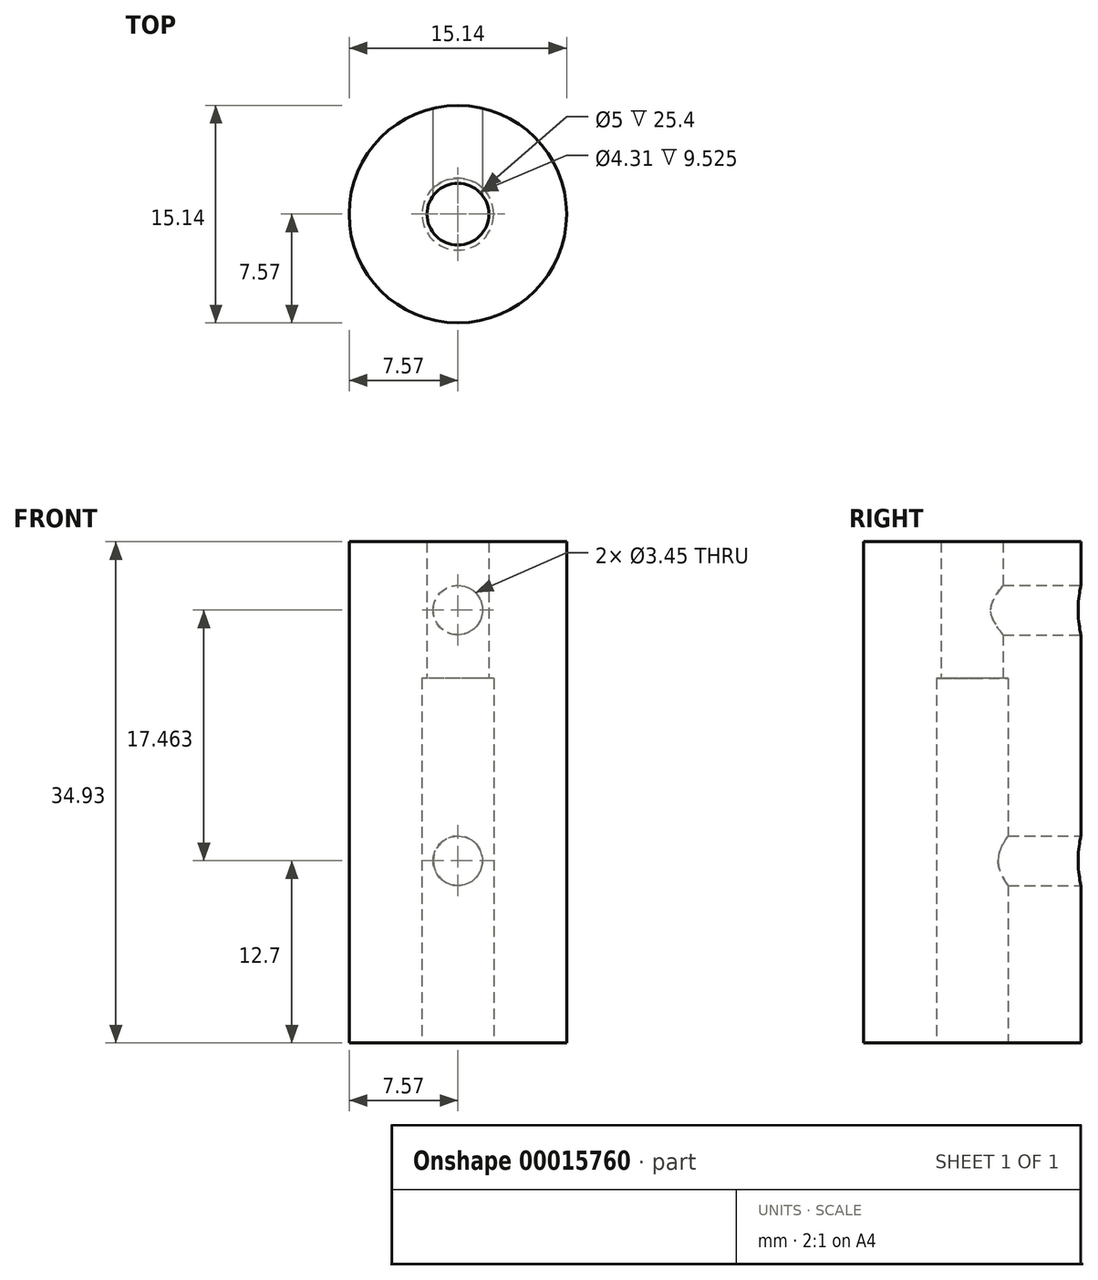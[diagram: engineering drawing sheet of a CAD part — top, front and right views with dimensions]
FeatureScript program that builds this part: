
annotation { "Feature Type Name" : "Feature", "Feature Type Description" : "" }
export const myFeature = defineFeature(function(context is Context, id is Id, definition is map)
    precondition{}
    {
        {
            var Q0;
            Q0=qCreatedBy(makeId("Top.planeOp"),FACE);
            var sketch = newSketch(context, id + "F0", { "sketchPlane" : qUnion([Q0])});
            skLineSegment(sketch, "E0.bottom", {"start": v(7.57, -7.57) * mm, "end": v(-7.57, -7.57) * mm});
            skLineSegment(sketch, "E0.top", {"start": v(7.57, 7.57) * mm, "end": v(-7.57, 7.57) * mm});
            skLineSegment(sketch, "E0.left", {"start": v(7.57, -7.57) * mm, "end": v(7.57, 7.57) * mm});
            skLineSegment(sketch, "E0.right", {"start": v(-7.57, -7.57) * mm, "end": v(-7.57, 7.57) * mm});
            skPoint(sketch, "E0.middle", {"position": v(0, 0) * mm});
            skCircle(sketch, "E1", {"center": v(0, 0) * mm, "radius": 7.57 * mm, "construction": true});
            skCircle(sketch, "E2", {"center": v(0, 0) * mm, "radius": 2.5 * mm});
            skLineSegment(sketch, "E3.bottom", {"start": v(2.15, 2.5) * mm, "end": v(-2.15, 2.5) * mm, "construction": true});
            skLineSegment(sketch, "E3.top", {"start": v(2.15, 7.26) * mm, "end": v(-2.15, 7.26) * mm, "construction": true});
            skLineSegment(sketch, "E3.left", {"start": v(2.15, 2.5) * mm, "end": v(2.15, 7.26) * mm, "construction": true});
            skLineSegment(sketch, "E3.right", {"start": v(-2.15, 2.5) * mm, "end": v(-2.15, 7.26) * mm, "construction": true});
            skSolve(sketch);
        }
        {
            var Q0;
            Q0 = qSketchRegion(id + "F0", true);
            extrude(context, id + "F1", {"entities" : qUnion([Q0]), "depth" : 25.4 * mm});
        }
        {
            var Q0;
            Q0=makeQuery(id+"F1.opExtrude","CAP_FACE",FACE,{"disambiguationData":[OSD([sQuery(id+"F0.wireOp",EDGE,"E0.bottom"),sQuery(id+"F0.wireOp",EDGE,"E0.top"),sQuery(id+"F0.wireOp",EDGE,"E0.left"),sQuery(id+"F0.wireOp",EDGE,"E0.right"),sQuery(id+"F0.wireOp",EDGE,"E2")])],"isStart":false});
            var sketch = newSketch(context, id + "F2", { "sketchPlane" : qUnion([Q0])});
            skLineSegment(sketch, "E4.bottom", {"start": v(7.57, 7.57) * mm, "end": v(-7.57, 7.57) * mm});
            skLineSegment(sketch, "E4.top", {"start": v(7.57, -7.57) * mm, "end": v(-7.57, -7.57) * mm});
            skLineSegment(sketch, "E4.left", {"start": v(7.57, 7.57) * mm, "end": v(7.57, -7.57) * mm});
            skLineSegment(sketch, "E4.right", {"start": v(-7.57, 7.57) * mm, "end": v(-7.57, -7.57) * mm});
            skPoint(sketch, "E4.middle", {"position": v(0, 0) * mm});
            skCircle(sketch, "E5", {"center": v(0, 0) * mm, "radius": 2.15 * mm});
            skSolve(sketch);
        }
        {
            var Q0;
            Q0 = qSketchRegion(id + "F2", true);
            extrude(context, id + "F3", {"entities" : qUnion([Q0]), "operationType" : NewBodyOperationType.ADD, "depth" : 9.52 * mm});
        }
        {
            var Q0;
            Q0=makeQuery(id+"F3.boolean.opBoolean","MERGE",FACE,{"derivedFrom":[makeQuery(id+"F1.opExtrude","SWEPT_FACE",FACE,{"disambiguationData":[OSD([sQuery(id+"F0.wireOp",EDGE,"E0.top")])]}),makeQuery(id+"F3.opExtrude","SWEPT_FACE",FACE,{"disambiguationData":[OSD([sQuery(id+"F2.wireOp",EDGE,"E4.bottom")])]})]});
            var sketch = newSketch(context, id + "F4", { "sketchPlane" : qUnion([Q0])});
            skLineSegment(sketch, "E6", {"start": v(0, 0) * mm, "end": v(0, 25.4) * mm, "construction": true});
            skLineSegment(sketch, "E7", {"start": v(0, 25.4) * mm, "end": v(0, 34.93) * mm, "construction": true});
            skCircle(sketch, "E8", {"center": v(0, 12.7) * mm, "radius": 1.73 * mm});
            skCircle(sketch, "E9", {"center": v(0, 30.16) * mm, "radius": 1.73 * mm});
            skSolve(sketch);
        }
        {
            var Q0;
            Q0 = qSketchRegion(id + "F4", true);
            var Q1;
            Q1=makeQuery(id+"F3.opExtrude","SWEPT_FACE",FACE,{"disambiguationData":[OSD([sQuery(id+"F2.wireOp",EDGE,"E5")])]});
            extrude(context, id + "F5", {"entities" : qUnion([Q0]), "operationType" : NewBodyOperationType.REMOVE, "endBound" : BoundingType.UP_TO_SURFACE, "oppositeDirection" : true, "endBoundEntityFace" : qUnion([Q1]), "depth" : 25.4 * mm});
        }
        {
            var Q0;
            Q0=makeQuery(id+"F3.boolean.opBoolean","MERGE",EDGE,{"derivedFrom":[makeQuery(id+"F1.opExtrude","SWEPT_EDGE",EDGE,{"disambiguationData":[OSD([sQuery(id+"F0.wireOp",EDGE,"E0.bottom"),sQuery(id+"F0.wireOp",EDGE,"E0.left")])]}),makeQuery(id+"F3.opExtrude","SWEPT_EDGE",EDGE,{"disambiguationData":[OSD([sQuery(id+"F2.wireOp",EDGE,"E4.top"),sQuery(id+"F2.wireOp",EDGE,"E4.left")])]})]});
            var Q1;
            Q1=makeQuery(id+"F3.boolean.opBoolean","MERGE",EDGE,{"derivedFrom":[makeQuery(id+"F1.opExtrude","SWEPT_EDGE",EDGE,{"disambiguationData":[OSD([sQuery(id+"F0.wireOp",EDGE,"E0.top"),sQuery(id+"F0.wireOp",EDGE,"E0.left")])]}),makeQuery(id+"F3.opExtrude","SWEPT_EDGE",EDGE,{"disambiguationData":[OSD([sQuery(id+"F2.wireOp",EDGE,"E4.bottom"),sQuery(id+"F2.wireOp",EDGE,"E4.left")])]})]});
            var Q2;
            Q2=makeQuery(id+"F3.boolean.opBoolean","MERGE",EDGE,{"derivedFrom":[makeQuery(id+"F1.opExtrude","SWEPT_EDGE",EDGE,{"disambiguationData":[OSD([sQuery(id+"F0.wireOp",EDGE,"E0.bottom"),sQuery(id+"F0.wireOp",EDGE,"E0.right")])]}),makeQuery(id+"F3.opExtrude","SWEPT_EDGE",EDGE,{"disambiguationData":[OSD([sQuery(id+"F2.wireOp",EDGE,"E4.top"),sQuery(id+"F2.wireOp",EDGE,"E4.right")])]})]});
            var Q3;
            Q3=makeQuery(id+"F3.boolean.opBoolean","MERGE",EDGE,{"derivedFrom":[makeQuery(id+"F1.opExtrude","SWEPT_EDGE",EDGE,{"disambiguationData":[OSD([sQuery(id+"F0.wireOp",EDGE,"E0.top"),sQuery(id+"F0.wireOp",EDGE,"E0.right")])]}),makeQuery(id+"F3.opExtrude","SWEPT_EDGE",EDGE,{"disambiguationData":[OSD([sQuery(id+"F2.wireOp",EDGE,"E4.bottom"),sQuery(id+"F2.wireOp",EDGE,"E4.right")])]})]});
            fillet(context, id + "F6", {"entities" : qUnion([Q0, Q1, Q2, Q3]), "radius" : 7.57 * mm, "tangentPropagation" : true, "allowEdgeOverflow" : false});
        }
    });
